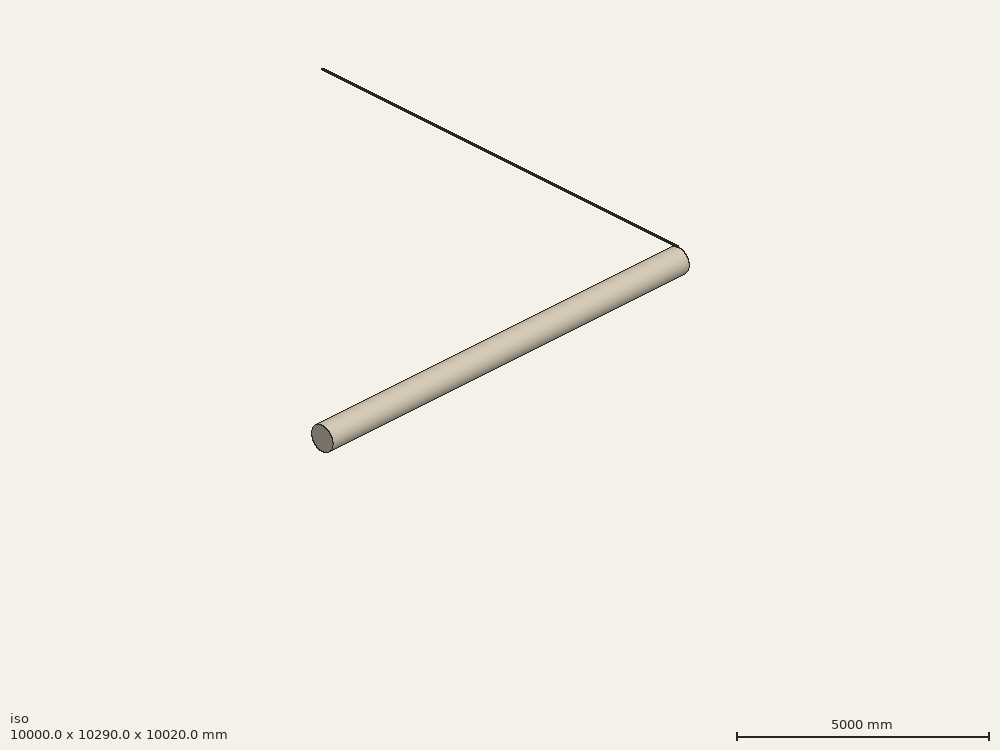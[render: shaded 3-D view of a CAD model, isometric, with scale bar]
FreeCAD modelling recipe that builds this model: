
FCSTD DOCUMENT  (FreeCAD 0.16R)
Label: Fender
License: All rights reserved
LicenseURL: http://en.wikipedia.org/wiki/All_rights_reserved
objects: Sketcher::SketchObject×8, PartDesign::Pocket×7, PartDesign::Fillet×2, PartDesign::Pad×1, PartDesign::Chamfer×1, Mesh::Feature×1
note: 27 computed .brp shape members not serialized (recipe doc carries the construction recipe); baked Part::Feature solids carry a one-line shape summary decoded from their .brp

FEATURE [Sketcher::SketchObject] Sketch
  sketch-geometry (4):
    g0: LineSegment StartX=-10 StartY=10 StartZ=0 EndX=10 EndY=10 EndZ=0
    g1: LineSegment StartX=10 StartY=10 StartZ=0 EndX=10 EndY=-10 EndZ=0
    g2: LineSegment StartX=10 StartY=-10 StartZ=0 EndX=-10 EndY=-10 EndZ=0
    g3: LineSegment StartX=-10 StartY=-10 StartZ=0 EndX=-10 EndY=10 EndZ=0
  constraints (11):
    c: Coincident(g0,g1)
    c: Coincident(g1,g2)
    c: Coincident(g2,g3)
    c: Coincident(g3,g0)
    c: Horizontal(g0)
    c: Horizontal(g2)
    c: Vertical(g1)
    c: Vertical(g3)
    c: Symmetric(g1,g0,g-1)
    c: Distance(g0) = 20
    c: Distance(g1) = 20
FEATURE [PartDesign::Pad] Pad
  Length = 20
  Length2 = 100
  Sketch = -> Sketch
  Type = 0
FEATURE [Sketcher::SketchObject] Sketch001
  Placement = pos=(0,-10,0) rot=(1,0,0;1.5708rad)
  Support = -> Pad [Face3]
  sketch-geometry (4):
    g0: LineSegment StartX=-15.9765 StartY=40 StartZ=0 EndX=-5 EndY=40 EndZ=0
    g1: LineSegment StartX=-5 StartY=40 StartZ=0 EndX=-5 EndY=5 EndZ=0
    g2: LineSegment StartX=-5 StartY=5 StartZ=0 EndX=-15.9765 EndY=5 EndZ=0
    g3: LineSegment StartX=-15.9765 StartY=5 StartZ=0 EndX=-15.9765 EndY=40 EndZ=0
  constraints (12):
    c: Coincident(g0,g1)
    c: Coincident(g1,g2)
    c: Coincident(g2,g3)
    c: Coincident(g3,g0)
    c: Horizontal(g0)
    c: Horizontal(g2)
    c: Vertical(g1)
    c: Vertical(g3)
    c: DistanceX(g0) = -5
    c: DistanceY(g1) = 5
    c: Distance(g0) = 10.9765
    c: DistanceY(g0) = 40
FEATURE [PartDesign::Pocket] Pocket
  Length = 5
  Sketch = -> Sketch001
  Type = 1
FEATURE [Sketcher::SketchObject] Sketch002
  Placement = pos=(10,0,0) rot=(0.57735,0.57735,0.57735;2.0944rad)
  Support = -> Pocket [Face3]
  sketch-geometry (1):
    g0: Circle CenterX=-5.26915 CenterY=15.5775 CenterZ=0 NormalX=0 NormalY=0 NormalZ=1 Radius=1.7
  constraints (1):
    c: Radius(g0) = 1.7
FEATURE [PartDesign::Pocket] Pocket001
  Length = 5
  Sketch = -> Sketch002
  Type = 1
FEATURE [Sketcher::SketchObject] Sketch003
  ExternalGeometry = -> [Pocket001]
  Placement = pos=(10,0,0) rot=(0.57735,0.57735,0.57735;2.0944rad)
  Support = -> Pocket001 [Face3]
  sketch-geometry (7):
    g0: LineSegment StartX=-4.3365 StartY=12.412 StartZ=0 EndX=-2.06145 EndY=14.8025 EndZ=0
    g1: LineSegment StartX=-2.06145 StartY=14.8025 StartZ=0 EndX=-2.9941 EndY=17.9679 EndZ=0
    g2: LineSegment StartX=-2.9941 StartY=17.9679 StartZ=0 EndX=-6.2018 EndY=18.743 EndZ=0
    g3: LineSegment StartX=-6.2018 StartY=18.743 StartZ=0 EndX=-8.47685 EndY=16.3525 EndZ=0
    g4: LineSegment StartX=-8.47685 StartY=16.3525 StartZ=0 EndX=-7.5442 EndY=13.1871 EndZ=0
    g5: LineSegment StartX=-7.5442 StartY=13.1871 StartZ=0 EndX=-4.3365 EndY=12.412 EndZ=0
    g6: Circle [constr] CenterX=-5.26915 CenterY=15.5775 CenterZ=0 NormalX=0 NormalY=0 NormalZ=1 Radius=3.3
  constraints (15):
    c: Coincident(g0,g1)
    c: Coincident(g1,g2)
    c: Coincident(g2,g3)
    c: Coincident(g3,g4)
    c: Coincident(g4,g5)
    c: Coincident(g5,g0)
    c: Equal(g0, g1-g5) x5
    c: PointOnObject(g0,g6)
    c: PointOnObject(g1,g6)
    c: PointOnObject(g2,g6)
    c: PointOnObject(g3,g6)
    c: PointOnObject(g4,g6)
    c: PointOnObject(g5,g6)
    c: Coincident(g6,g-3)
    c: Radius(g6) = 3.3
FEATURE [PartDesign::Pocket] Pocket002
  Length = 6
  Sketch = -> Sketch003
  Type = 0
FEATURE [PartDesign::Fillet] Fillet
  Base = -> Pocket002 [Edge19,Edge3]
  Radius = 6
FEATURE [Sketcher::SketchObject] Sketch004
  ExternalGeometry = -> [Fillet]
  Placement = pos=(0,-10,0) rot=(1,0,0;1.5708rad)
  Support = -> Fillet [Face9]
  sketch-geometry (3):
    g0: ArcOfCircle CenterX=0 CenterY=-50 CenterZ=0 NormalX=0 NormalY=0 NormalZ=1 Radius=50.9902 StartAngle=1.3734 EndAngle=1.76819
    g1: LineSegment StartX=-10 StartY=0 StartZ=0 EndX=9.98951 EndY=-0.024184 EndZ=0
    g2: LineSegment StartX=9.98951 StartY=-0.024184 StartZ=0 EndX=10 EndY=0 EndZ=0
  constraints (7):
    c: PointOnObject(g0,g-2)
    c: DistanceY(g0) = -50
    c: Coincident(g0,g-4)
    c: PointOnObject(g0,g-1)
    c: Coincident(g0,g1)
    c: Coincident(g1,g2)
    c: Coincident(g2,g0)
FEATURE [PartDesign::Pocket] Pocket003
  Length = 5
  Sketch = -> Sketch004
  Type = 1
FEATURE [Sketcher::SketchObject] Sketch006
  ExternalGeometry = -> [Pocket003]
  Placement = pos=(10,0,0) rot=(0.57735,0.57735,0.57735;2.0944rad)
  Support = -> Pocket003 [Face7]
  sketch-geometry (1):
    g0: Circle CenterX=0 CenterY=-299.833 CenterZ=0 NormalX=0 NormalY=0 NormalZ=1 Radius=300
  constraints (3):
    c: PointOnObject(g0,g-2)
    c: PointOnObject(g-3,g0)
    c: Radius(g0) = 300
FEATURE [PartDesign::Pocket] Pocket004
  Length = 5
  Sketch = -> Sketch006
  Type = 1
FEATURE [Sketcher::SketchObject] Sketch007
  Placement = pos=(0,0,20) rot=(0,0,1;0rad)
  Support = -> Pocket004 [Face8]
  sketch-geometry (4):
    g0: LineSegment StartX=0 StartY=3.96985 StartZ=0 EndX=-2.96985 EndY=1 EndZ=0
    g1: LineSegment StartX=-2.96985 StartY=1 StartZ=0 EndX=0 EndY=-1.96985 EndZ=0
    g2: LineSegment StartX=0 StartY=-1.96985 StartZ=0 EndX=2.96985 EndY=1 EndZ=0
    g3: LineSegment StartX=2.96985 StartY=1 StartZ=0 EndX=0 EndY=3.96985 EndZ=0
  constraints (12):
    c: Coincident(g0,g1)
    c: Coincident(g1,g2)
    c: Coincident(g2,g3)
    c: Coincident(g3,g0)
    c: Perpendicular(g0,g3)
    c: Perpendicular(g3,g2)
    c: Equal(g1,g0)
    c: Perpendicular(g0,g1)
    c: Distance(g3) = 4.2
    c: PointOnObject(g0,g-2)
    c: Symmetric(g2,g0,g-2)
    c: DistanceY(g2) = 1
FEATURE [PartDesign::Pocket] Pocket005
  Length = 5
  Sketch = -> Sketch007
  Type = 1
FEATURE [Sketcher::SketchObject] Sketch008
  Placement = pos=(0,0,20) rot=(0,0,1;0rad)
  Support = -> Pocket005 [Face8]
  sketch-geometry (5):
    g0: LineSegment StartX=-5.87846 StartY=-2.6 StartZ=0 EndX=2.12154 EndY=-2.6 EndZ=0
    g1: LineSegment StartX=2.12154 StartY=-2.6 StartZ=0 EndX=4.2 EndY=1 EndZ=0
    g2: LineSegment StartX=4.2 StartY=1 StartZ=0 EndX=2.12154 EndY=4.6 EndZ=0
    g3: LineSegment StartX=2.12154 StartY=4.6 StartZ=0 EndX=-5.87846 EndY=4.6 EndZ=0
    g4: LineSegment StartX=-5.87846 StartY=4.6 StartZ=0 EndX=-5.87846 EndY=-2.6 EndZ=0
  constraints (15):
    c: Coincident(g0,g1)
    c: Coincident(g1,g2)
    c: Coincident(g2,g3)
    c: Horizontal(g3)
    c: Angle(g3,g2) = 2.0944
    c: Angle(g2,g1) = 2.0944
    c: Angle(g1,g0) = 2.0944
    c: Distance(g2,g0) = 7.2
    c: Equal(g2,g1)
    c: Coincident(g4,g3)
    c: Coincident(g4,g0)
    c: Vertical(g4)
    c: Distance(g0) = 8
    c: DistanceY(g2) = 4.6
    c: DistanceX(g1) = 4.2
FEATURE [PartDesign::Pocket] Pocket006
  Length = 7
  Sketch = -> Sketch008
  Type = 0
FEATURE [PartDesign::Fillet] Fillet001
  Base = -> Pocket006 [Edge62,Edge59,Edge61]
  Radius = 1.8
FEATURE [PartDesign::Chamfer] Chamfer
  Base = -> Fillet001 [Edge79,Edge75,Edge81,Edge78,Edge74,Edge71]
  Size = 1.1
FEATURE [Mesh::Feature] Mesh  label="Chamfer (Meshed)"
